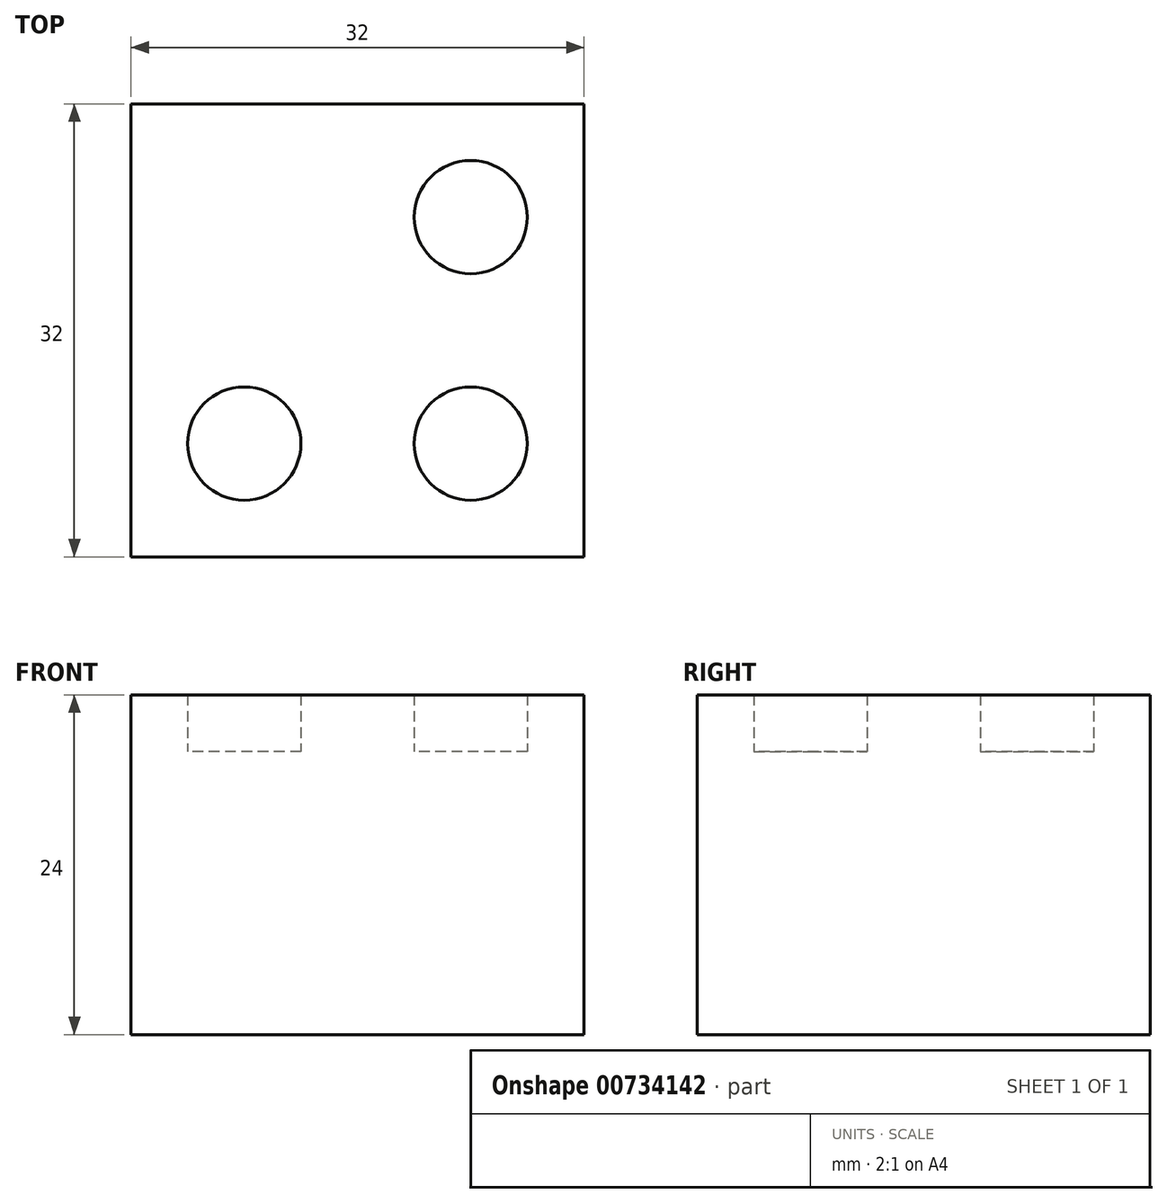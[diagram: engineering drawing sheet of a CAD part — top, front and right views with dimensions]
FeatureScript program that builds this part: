
annotation { "Feature Type Name" : "Feature", "Feature Type Description" : "" }
export const myFeature = defineFeature(function(context is Context, id is Id, definition is map)
    precondition{}
    {
        {
            var Q0;
            Q0=qCreatedBy(makeId("Top.planeOp"),FACE);
            var sketch = newSketch(context, id + "F0", { "sketchPlane" : qUnion([Q0])});
            skLineSegment(sketch, "E0.bottom", {"start": v(5.82, 10.5) * mm, "end": v(37.82, 10.5) * mm});
            skLineSegment(sketch, "E0.top", {"start": v(5.82, -21.5) * mm, "end": v(37.82, -21.5) * mm});
            skLineSegment(sketch, "E0.left", {"start": v(5.82, 10.5) * mm, "end": v(5.82, -21.5) * mm});
            skLineSegment(sketch, "E0.right", {"start": v(37.82, 10.5) * mm, "end": v(37.82, -21.5) * mm});
            skSolve(sketch);
        }
        {
            var Q0;
            Q0 = qSketchRegion(id + "F0", true);
            extrude(context, id + "F1", {"entities" : qUnion([Q0]), "depth" : 20 * mm, "offsetDistance" : 25 * mm});
        }
        {
            var Q0;
            Q0=makeQuery(id+"F1.opExtrude","CAP_FACE",FACE,{"disambiguationData":[OSD([sQuery(id+"F0.wireOp",EDGE,"E0.bottom"),sQuery(id+"F0.wireOp",EDGE,"E0.top"),sQuery(id+"F0.wireOp",EDGE,"E0.left"),sQuery(id+"F0.wireOp",EDGE,"E0.right")])],"isStart":false});
            var sketch = newSketch(context, id + "F2", { "sketchPlane" : qUnion([Q0])});
            skCircle(sketch, "E1", {"center": v(13.82, 2.5) * mm, "radius": 4 * mm});
            skSolve(sketch);
        }
        {
            var Q0;
            Q0=sQuery(id+"F2.wireOp",EDGE,"E1");
            extrude(context, id + "F3", {"bodyType" : ToolBodyType.SURFACE, "surfaceEntities" : qUnion([Q0]), "depth" : 4 * mm, "offsetDistance" : 25 * mm});
        }
        {
            var Q0;
            Q0=makeQuery(id+"F1.opExtrude","CAP_FACE",FACE,{"disambiguationData":[OSD([sQuery(id+"F0.wireOp",EDGE,"E0.bottom"),sQuery(id+"F0.wireOp",EDGE,"E0.top"),sQuery(id+"F0.wireOp",EDGE,"E0.left"),sQuery(id+"F0.wireOp",EDGE,"E0.right")])],"isStart":false});
            var sketch = newSketch(context, id + "F4", { "sketchPlane" : qUnion([Q0])});
            skCircle(sketch, "E2", {"center": v(29.82, 2.5) * mm, "radius": 4 * mm});
            skCircle(sketch, "E3", {"center": v(13.82, -13.5) * mm, "radius": 4 * mm});
            skCircle(sketch, "E4", {"center": v(29.82, -13.5) * mm, "radius": 4 * mm});
            skSolve(sketch);
        }
        {
            var Q0;
            Q0=makeQuery(id+"F4.imprint","IMPRINT",FACE,{"disambiguationData":[TD([[makeQuery(id+"F4.imprint","IMPRINT",EDGE,{"derivedFrom":sQuery(id+"F4.wireOp",EDGE,"E2")}),-1.0]])]});
            extrude(context, id + "F5", {"entities" : qUnion([Q0]), "operationType" : NewBodyOperationType.ADD, "depth" : 4 * mm, "offsetDistance" : 25 * mm});
        }
    });
